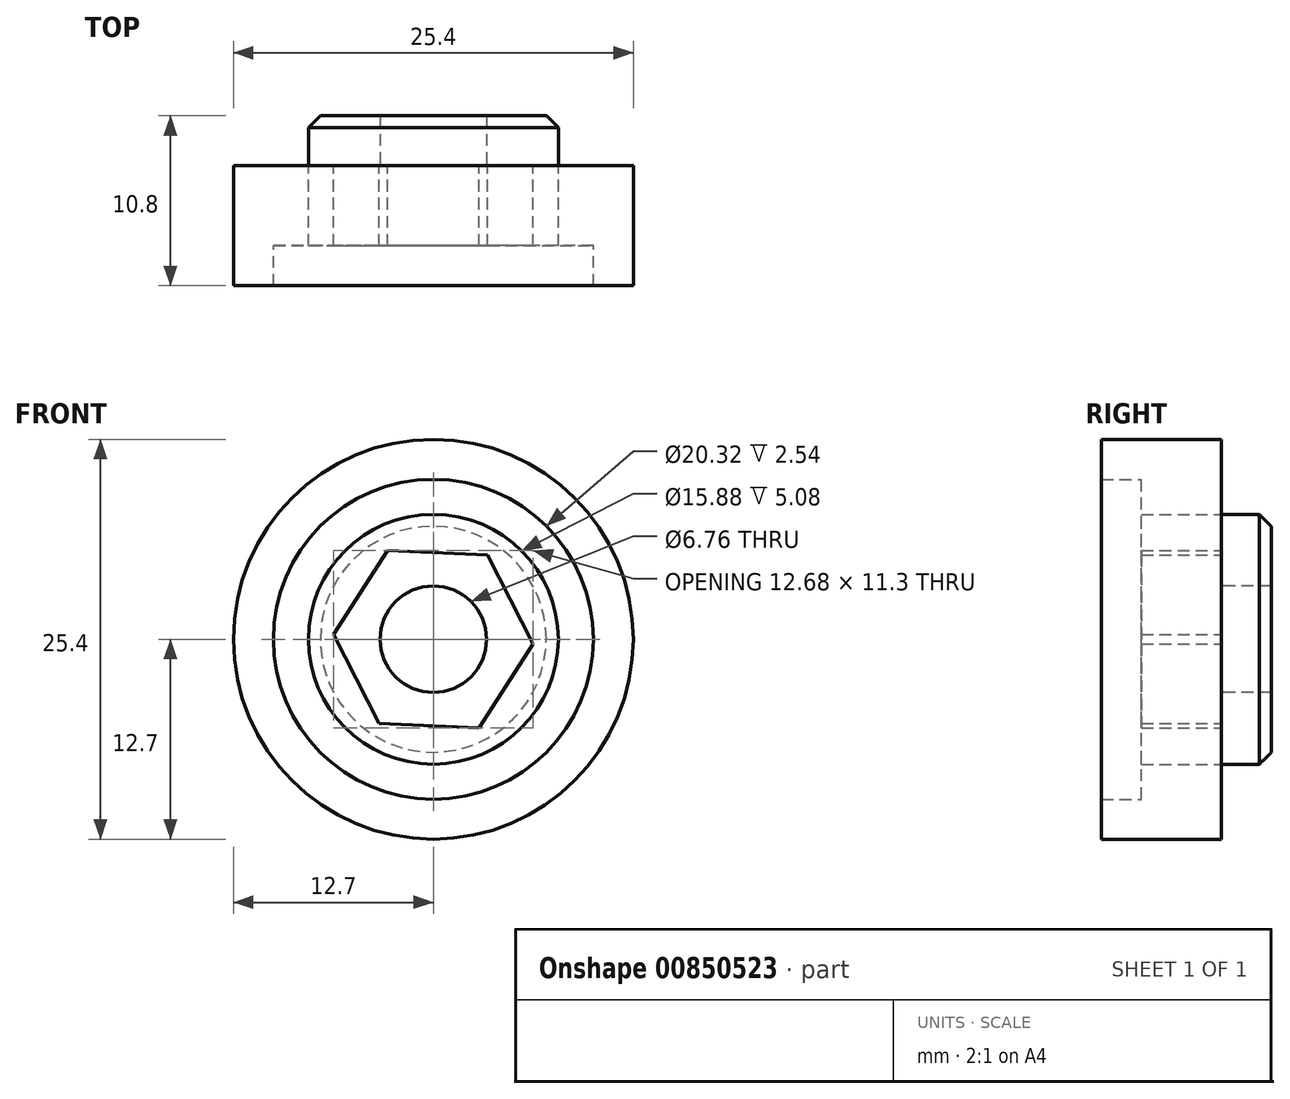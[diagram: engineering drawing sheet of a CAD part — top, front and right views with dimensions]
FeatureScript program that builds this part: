
annotation { "Feature Type Name" : "Feature", "Feature Type Description" : "" }
export const myFeature = defineFeature(function(context is Context, id is Id, definition is map)
    precondition{}
    {
        {
            var Q0;
            Q0=qCreatedBy(makeId("Front.planeOp"),FACE);
            var sketch = newSketch(context, id + "F0", { "sketchPlane" : qUnion([Q0])});
            skCircle(sketch, "E0", {"center": v(0, 0) * mm, "radius": 3.38 * mm});
            skCircle(sketch, "E1.cCircle", {"center": v(0, 0) * mm, "radius": 5.5 * mm, "construction": true});
            skLineSegment(sketch, "E1.0", {"start": v(-6.34, 0.31) * mm, "end": v(-2.9, 5.65) * mm});
            skLineSegment(sketch, "E1.1", {"start": v(-2.9, 5.65) * mm, "end": v(3.44, 5.34) * mm});
            skLineSegment(sketch, "E1.2", {"start": v(3.44, 5.34) * mm, "end": v(6.34, -0.31) * mm});
            skLineSegment(sketch, "E1.3", {"start": v(6.34, -0.31) * mm, "end": v(2.9, -5.65) * mm});
            skLineSegment(sketch, "E1.4", {"start": v(2.9, -5.65) * mm, "end": v(-3.44, -5.34) * mm});
            skLineSegment(sketch, "E1.5", {"start": v(-3.44, -5.34) * mm, "end": v(-6.34, 0.31) * mm});
            skPoint(sketch, "E1.0.midPoint", {"position": v(-4.62, 2.98) * mm});
            skCircle(sketch, "E2", {"center": v(0, 0) * mm, "radius": 7.94 * mm});
            skCircle(sketch, "E3", {"center": v(0, 0) * mm, "radius": 10.16 * mm});
            skCircle(sketch, "E4", {"center": v(0, 0) * mm, "radius": 12.7 * mm});
            skSolve(sketch);
        }
        {
            var Q0;
            Q0=makeQuery(id+"F0.imprint","IMPRINT",FACE,{"disambiguationData":[TD([[makeQuery(id+"F0.imprint","IMPRINT",EDGE,{"derivedFrom":sQuery(id+"F0.wireOp",EDGE,"E0")}),-1.0]])]});
            var Q1;
            Q1=makeQuery(id+"F0.imprint","IMPRINT",FACE,{"disambiguationData":[TD([[makeQuery(id+"F0.imprint","IMPRINT",EDGE,{"derivedFrom":sQuery(id+"F0.wireOp",EDGE,"E1.0")}),1.0]])]});
            var Q2;
            Q2=sQuery(id+"F0.wireOp",EDGE,"E4");
            extrude(context, id + "F1", {"entities" : qUnion([Q0, Q1]), "surfaceEntities" : qUnion([Q2]), "oppositeDirection" : true, "depth" : 3.17 * mm, "offsetDistance" : 25.4 * mm});
        }
        {
            var Q0;
            Q0=makeQuery(id+"F0.imprint","IMPRINT",FACE,{"disambiguationData":[TD([[makeQuery(id+"F0.imprint","IMPRINT",EDGE,{"derivedFrom":sQuery(id+"F0.wireOp",EDGE,"E3")}),-1.0]])]});
            var Q1;
            Q1=sQuery(id+"F0.wireOp",EDGE,"E4");
            extrude(context, id + "F2", {"entities" : qUnion([Q0]), "surfaceEntities" : qUnion([Q1]), "depth" : 7.62 * mm, "offsetDistance" : 25.4 * mm});
        }
        {
            var Q0;
            Q0=makeQuery(id+"F0.imprint","IMPRINT",FACE,{"disambiguationData":[TD([[makeQuery(id+"F0.imprint","IMPRINT",EDGE,{"derivedFrom":sQuery(id+"F0.wireOp",EDGE,"E2")}),-1.0]])]});
            var Q1;
            Q1=sQuery(id+"F0.wireOp",EDGE,"E3");
            var Q2;
            Q2=sQuery(id+"F0.wireOp",EDGE,"E2");
            extrude(context, id + "F3", {"entities" : qUnion([Q0]), "operationType" : NewBodyOperationType.ADD, "surfaceEntities" : qUnion([Q1, Q2]), "depth" : 5.08 * mm, "offsetDistance" : 25.4 * mm});
        }
        {
            var Q0;
            Q0=makeQuery(id+"F0.imprint","IMPRINT",FACE,{"disambiguationData":[TD([[makeQuery(id+"F0.imprint","IMPRINT",EDGE,{"derivedFrom":sQuery(id+"F0.wireOp",EDGE,"E1.0")}),1.0]])]});
            var Q1;
            Q1=sQuery(id+"F0.wireOp",EDGE,"E0");
            var Q2;
            Q2=sQuery(id+"F0.wireOp",EDGE,"E2");
            extrude(context, id + "F4", {"entities" : qUnion([Q0]), "surfaceEntities" : qUnion([Q1, Q2]), "depth" : 5.08 * mm, "offsetDistance" : 25.4 * mm});
        }
        {
            var Q0;
            Q0=makeQuery(id+"F1.opExtrude","CAP_EDGE",EDGE,{"disambiguationData":[OSD([sQuery(id+"F0.wireOp",EDGE,"E2")])],"isStart":false});
            chamfer(context, id + "F5", {"entities" : qUnion([Q0]), "width" : 0.76 * mm, "tangentPropagation" : true});
        }
    });
